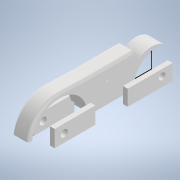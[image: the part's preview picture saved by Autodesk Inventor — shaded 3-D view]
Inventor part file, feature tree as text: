
AUTODESK INVENTOR PART (.ipt)
format: ipt  version: 2021.1 (Build 251245000, 245)  size: 195,072 bytes
history: native  units: in
note: dims shown in document units (in); Inventor stores cm internally (conversion verified against a paired STEP export)
features: sketch x6, extrude x5, fillet x1
ambient origin geometry x8: Origin, YZ Plane, XZ Plane, XY Plane, X Axis, Y Axis, Z Axis, Center Point
bodies: Solid1 (feature_tree)
feature tree (12):
  extrude  "Extrusion1"  Depth=5.3125in
  fillet  "Fillet1"  Radius=5.3125in
  extrude  "Extrusion2"  Depth=5.3125in TaperAngle=0.0deg
  sketch  "Sketch3"  dims[d11=5.3125in d12=0.0in]
  extrude  "Extrusion3"  [1 undecoded]
  extrude  "Extrusion4"  [1 undecoded]
  extrude  "Extrusion5"  [1 undecoded]
  sketch  "Sketch1"  dims[d2=18.0in d3=0.0in d4=3.0in d5=5.3125in d6=0.0in]
  sketch  "Sketch2"  dims[d7=5.3125in d8=0.0in d9=5.3125in d10=0.0in]
  sketch  "Sketch4"
  sketch  "Sketch5"
  sketch  "Sketch6"
note: 3 required parameter values undecoded (feature->parameter linkage not recoverable at this tier; creation-order binding heuristic only, values carry confidence <= 0.55)
